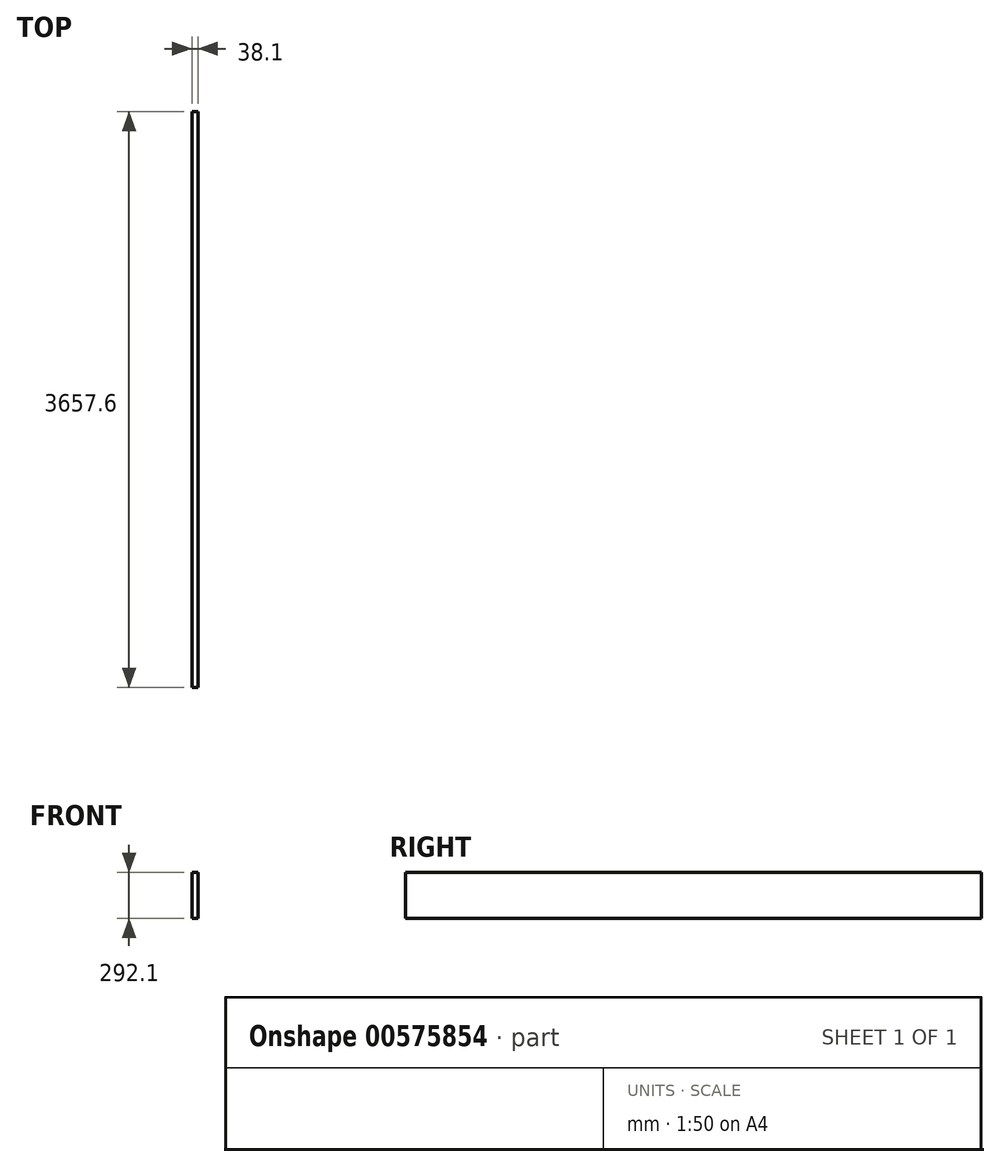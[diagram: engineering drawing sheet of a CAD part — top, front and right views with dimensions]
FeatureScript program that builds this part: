
annotation { "Feature Type Name" : "Feature", "Feature Type Description" : "" }
export const myFeature = defineFeature(function(context is Context, id is Id, definition is map)
    precondition{}
    {
        {
            var Q0;
            Q0=qCreatedBy(makeId("Front.planeOp"),FACE);
            var sketch = newSketch(context, id + "F0", { "sketchPlane" : qUnion([Q0])});
            skLineSegment(sketch, "E0.bottom", {"start": v(0, 0) * mm, "end": v(38.1, 0) * mm});
            skLineSegment(sketch, "E0.top", {"start": v(0, 292.1) * mm, "end": v(38.1, 292.1) * mm});
            skLineSegment(sketch, "E0.left", {"start": v(0, 0) * mm, "end": v(0, 292.1) * mm});
            skLineSegment(sketch, "E0.right", {"start": v(38.1, 0) * mm, "end": v(38.1, 292.1) * mm});
            skSolve(sketch);
        }
        {
            var Q0;
            Q0 = qSketchRegion(id + "F0", true);
            extrude(context, id + "F1", {"entities" : qUnion([Q0]), "depth" : 3657.6 * mm, "offsetDistance" : 25.4 * mm});
        }
    });
